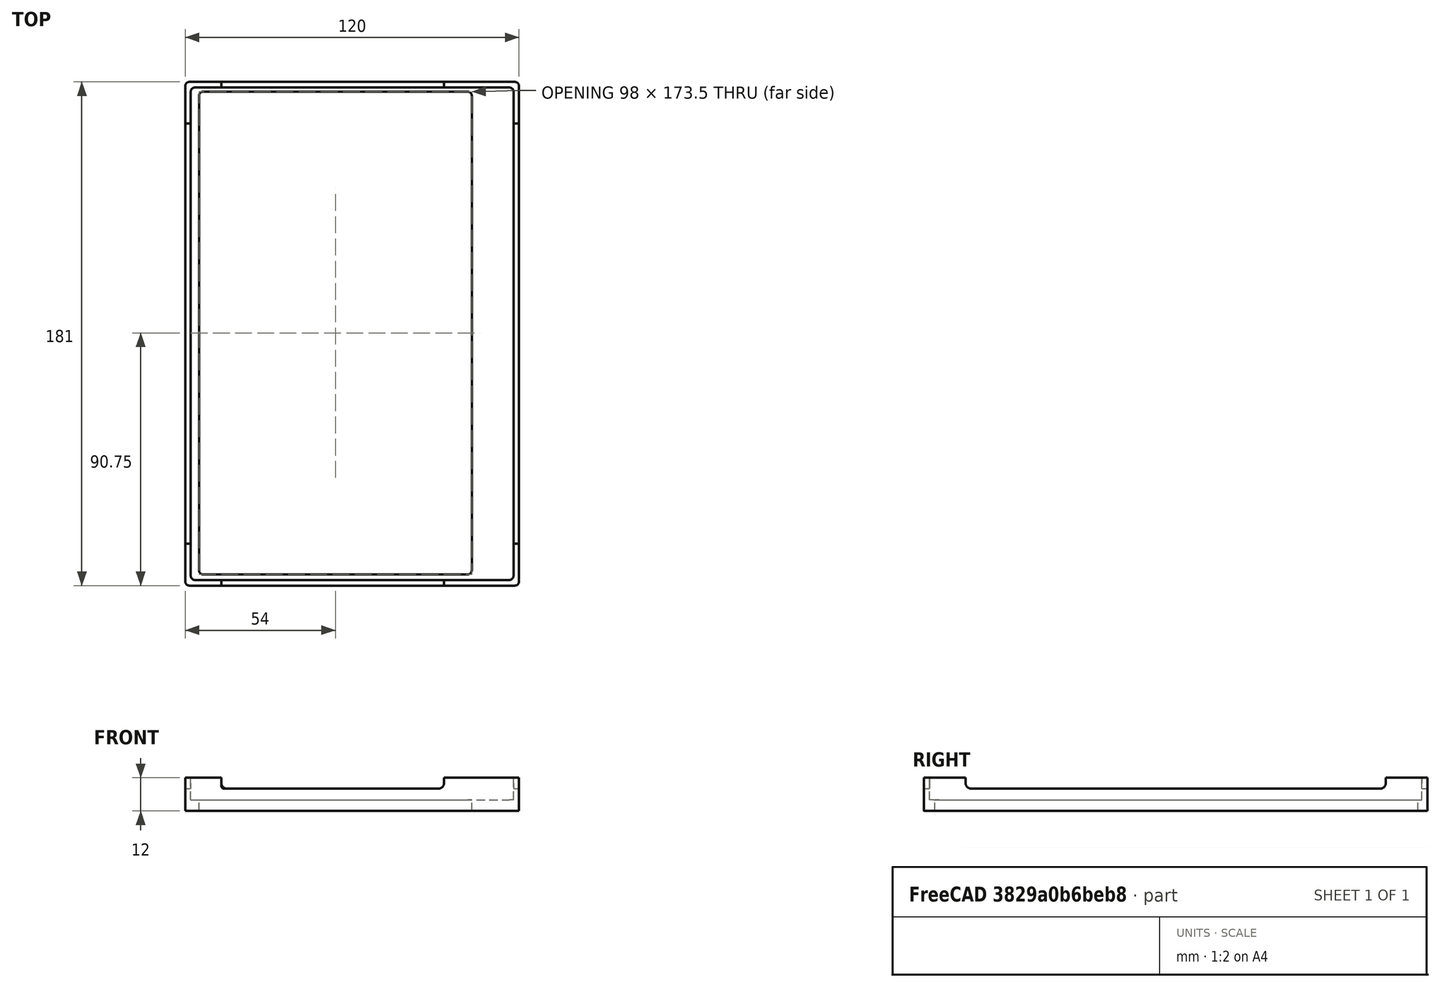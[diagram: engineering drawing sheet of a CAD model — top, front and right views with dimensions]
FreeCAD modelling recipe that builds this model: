
FCSTD DOCUMENT  (FreeCAD 0.20R29177 (Git))
Label: carrier-atoto-s8_test_F
License: All rights reserved
LicenseURL: http://en.wikipedia.org/wiki/All_rights_reserved
objects: Part::Box×8, Part::Fillet×5, Part::Cut×3, Part::MultiFuse×2
note: 18 computed .brp shape members not serialized (recipe doc carries the construction recipe); baked Part::Feature solids carry a one-line shape summary decoded from their .brp

FEATURE [Part::Box] Box  label="Cube"
  AttacherType = Attacher::AttachEngine3D
  Height = 4
  Length = 120
  Placement = pos=(2,0,0) rot=(0,0,1;0rad)
  Width = 181
FEATURE [Part::Box] Box001  label="Cube001"
  AttacherType = Attacher::AttachEngine3D
  Height = 4
  Length = 98
  Placement = pos=(7,4,0) rot=(0,0,1;0rad)
  Width = 173.5
FEATURE [Part::Fillet] Fillet
  Base = -> Box001
  Edges = 4 edges r=1.5: [Edge1,Edge3,Edge5,Edge7]
FEATURE [Part::Fillet] Fillet001
  Base = -> Box
  Edges = 4 edges r=1.5: [Edge1,Edge3,Edge5,Edge7]
FEATURE [Part::Cut] Cut
  Base = -> Fillet001
  Tool = -> Fillet
FEATURE [Part::Box] Box002  label="Cube002"
  AttacherType = Attacher::AttachEngine3D
  Height = 8
  Length = 120
  Placement = pos=(2,0,4) rot=(0,0,1;0rad)
  Width = 181
FEATURE [Part::Box] Box003  label="Cube003"
  AttacherType = Attacher::AttachEngine3D
  Height = 10
  Length = 116
  Placement = pos=(4,2,4) rot=(0,0,1;0rad)
  Width = 177
FEATURE [Part::Fillet] Fillet002
  Base = -> Box003
  Edges = 4 edges r=1.5: [Edge1,Edge3,Edge5,Edge7]
FEATURE [Part::Fillet] Fillet003
  Base = -> Box002
  Edges = 4 edges r=1.5: [Edge1,Edge3,Edge5,Edge7]
FEATURE [Part::Cut] Cut001
  Base = -> Fillet003
  Tool = -> Fillet002
FEATURE [Part::Box] Box004  label="Cube004"
  AttacherType = Attacher::AttachEngine3D
  Height = 10
  Length = 10
  Placement = pos=(115,15,0) rot=(0,0,1;0rad)
  Width = 151
FEATURE [Part::Box] Box005  label="Cube005"
  AttacherType = Attacher::AttachEngine3D
  Height = 10
  Length = 10
  Placement = pos=(0,15,0) rot=(0,0,1;0rad)
  Width = 151
FEATURE [Part::Box] Box006  label="Cube006"
  AttacherType = Attacher::AttachEngine3D
  Height = 10
  Length = 80
  Placement = pos=(15,-5,0) rot=(0,0,1;0rad)
  Width = 10
FEATURE [Part::Box] Box007  label="Cube007"
  AttacherType = Attacher::AttachEngine3D
  Height = 10
  Length = 80
  Placement = pos=(15,175,0) rot=(0,0,1;0rad)
  Width = 10
FEATURE [Part::MultiFuse] Fusion
  Placement = pos=(0,0,8) rot=(0,0,1;0rad)
  Shapes = -> [Box007,Box004,Box006,Box005]
FEATURE [Part::Fillet] Fillet004
  Base = -> Fusion
  Edges = 8 edges: [Edge4 r=2,Edge8 r=2,Edge21 r=2,Edge23 r=2,Edge28 r=1,Edge32 r=2,Edge45 r=2,Edge47 r=2]
FEATURE [Part::Cut] Cut002
  Base = -> Cut001
  Tool = -> Fillet004
FEATURE [Part::MultiFuse] Fusion001
  Shapes = -> [Cut,Cut002]
